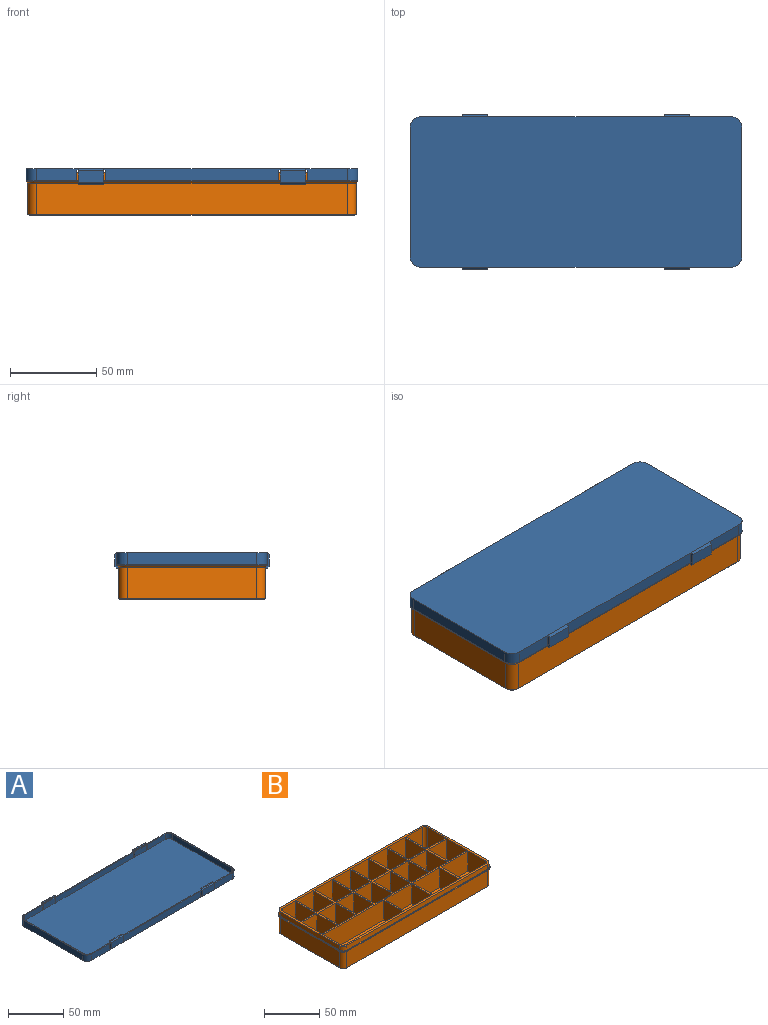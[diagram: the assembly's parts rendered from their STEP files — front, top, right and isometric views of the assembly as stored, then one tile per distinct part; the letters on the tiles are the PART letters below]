
ASSEMBLY  parts=2 mates=1
PART A: 82 faces, bbox 192x89.4x9 mm
  f0: plane 6x1mm, normal (-1,0,0), area 6mm2, adj f14,f18,f39,f43
  f1: plane 6x1mm, normal (1,0,0), area 6mm2, adj f21,f24,f30,f43
  f2: plane 6x1mm, normal (1,0,0), area 6mm2, adj f21,f29,f31,f43
  f3: plane 6x1mm, normal (-1,0,0), area 6mm2, adj f17,f18,f41,f43
  f4: plane 9x2.2mm, normal (-1,0,0), area 16.7mm2, adj f13,f28,f31,f43,f54,f58,f63,f75
  f5: plane 9x2.2mm, normal (1,0,0), area 16.7mm2, adj f13,f16,f28,f43,f54,f58,f63,f75
  f6: plane 9x2.2mm, normal (-1,0,0), area 16.7mm2, adj f12,f16,f26,f43,f55,f59,f62,f72
  f7: plane 6x1mm, normal (-1,0,0), area 6mm2, adj f16,f19,f27,f43
  f8: plane 6x1mm, normal (1,0,0), area 6mm2, adj f16,f19,f27,f43
  f9: plane 9x2.2mm, normal (1,0,0), area 16.7mm2, adj f12,f17,f26,f43,f55,f59,f62,f72
  f10: plane 15x0.6mm, normal (0,1,0), area 9mm2, adj f49,f52,f56,f68
  f11: plane 15x0.6mm, normal (0,1,0), area 9mm2, adj f48,f50,f57,f69
  f12: plane 15x0.6mm, normal (0,-1,0), area 9mm2, adj f6,f9,f55,f73
  f13: plane 15x0.6mm, normal (0,-1,0), area 9mm2, adj f4,f5,f54,f76
  f14: plane 24x7mm, normal (0,-1,0), area 162mm2, adj f0,f18,f34,f35,f43,f48
  f15: plane 102x7mm, normal (0,-1,0), area 702mm2, adj f20,f34,f43,f50,f51,f52,f53
  f16: plane 102x7mm, normal (0,1,0), area 702mm2, adj f5,f6,f7,f8,f19,f34,f43
  f17: plane 24x7mm, normal (0,1,0), area 162mm2, adj f3,f9,f18,f34,f36,f43
  f18: plane 87x29mm, normal (0,0,1), area 138.3mm2, adj f0,f3,f14,f17,f32,f35,f36,f39
  f19: plane 100x1mm, normal (0,0,1), area 100mm2, adj f7,f8,f16,f27
  f20: plane 100x1mm, normal (0,0,1), area 100mm2, adj f15,f23,f51,f53
  f21: plane 87x29mm, normal (0,0,1), area 138.3mm2, adj f1,f2,f24,f29,f30,f31,f33,f37
  f22: plane 15x6mm, normal (0,1,0), area 90mm2, adj f43,f49,f52,f66
  f23: plane 100x6mm, normal (0,1,0), area 600mm2, adj f20,f43,f51,f53
  f24: plane 23x6mm, normal (0,1,0), area 138mm2, adj f1,f21,f43,f47
  f25: plane 15x6mm, normal (0,1,0), area 90mm2, adj f43,f48,f50,f71
  f26: plane 15x6mm, normal (0,-1,0), area 90mm2, adj f6,f9,f43,f74
  f27: plane 100x6mm, normal (0,-1,0), area 600mm2, adj f7,f8,f19,f43
  f28: plane 15x6mm, normal (0,-1,0), area 90mm2, adj f4,f5,f43,f75
  f29: plane 23x6mm, normal (0,-1,0), area 138mm2, adj f2,f21,f43,f46
  f30: plane 24x7mm, normal (0,-1,0), area 162mm2, adj f1,f21,f34,f38,f43,f49
  f31: plane 24x7mm, normal (0,1,0), area 162mm2, adj f2,f4,f21,f34,f37,f43
  f32: plane 75x7mm, normal (1,0,0), area 525mm2, adj f18,f34,f35,f36
  f33: plane 75x7mm, normal (-1,0,0), area 525mm2, adj f21,f34,f37,f38
  f34: plane 192x87mm, normal (0,0,-1), area 16673.1mm2, adj f14,f15,f16,f17,f30,f31,f32,f33
  f35: cylinder r=6mm len=7mm, axis (0,0,1), area 66mm2, adj f14,f18,f32,f34
  f36: cylinder r=6mm len=7mm, axis (0,0,-1), area 66mm2, adj f17,f18,f32,f34
  f37: cylinder r=6mm len=7mm, axis (0,0,1), area 66mm2, adj f21,f31,f33,f34
  f38: cylinder r=6mm len=7mm, axis (0,0,-1), area 66mm2, adj f21,f30,f33,f34
  f39: plane 23x6mm, normal (0,1,0), area 138mm2, adj f0,f18,f43,f44
  f40: plane 75x6mm, normal (-1,0,0), area 450mm2, adj f18,f43,f44,f45
  f41: plane 23x6mm, normal (0,-1,0), area 138mm2, adj f3,f18,f43,f45
  f42: plane 75x6mm, normal (1,0,0), area 450mm2, adj f21,f43,f46,f47
  f43: plane 190x87mm, normal (0,0,1), area 16136.5mm2, adj f0,f1,f2,f3,f4,f5,f6,f7
  f44: cylinder r=5mm len=6mm, axis (0,0,1), area 47.1mm2, adj f18,f39,f40,f43
  f45: cylinder r=5mm len=6mm, axis (0,0,-1), area 47.1mm2, adj f18,f40,f41,f43
  f46: cylinder r=5mm len=6mm, axis (0,0,1), area 47.1mm2, adj f21,f29,f42,f43
  f47: cylinder r=5mm len=6mm, axis (0,0,-1), area 47.1mm2, adj f21,f24,f42,f43
  f48: plane 9x2.2mm, normal (1,0,0), area 16.7mm2, adj f11,f14,f25,f43,f57,f61,f64,f69
  f49: plane 9x2.2mm, normal (-1,0,0), area 16.7mm2, adj f10,f22,f30,f43,f56,f60,f65,f66
  f50: plane 9x2.2mm, normal (-1,0,0), area 16.7mm2, adj f11,f15,f25,f43,f57,f61,f64,f69
  f51: plane 6x1mm, normal (1,0,0), area 6mm2, adj f15,f20,f23,f43
  f52: plane 9x2.2mm, normal (1,0,0), area 16.7mm2, adj f10,f15,f22,f43,f56,f60,f65,f66
  f53: plane 6x1mm, normal (-1,0,0), area 6mm2, adj f15,f20,f23,f43
  f54: plane 15x1.2mm, normal (0,0,1), area 18mm2, adj f4,f5,f13,f78
  f55: plane 15x1.2mm, normal (0,0,1), area 18mm2, adj f6,f9,f12,f79
  f56: plane 15x1.2mm, normal (0,0,1), area 18mm2, adj f10,f49,f52,f80
  f57: plane 15x1.2mm, normal (0,0,1), area 18mm2, adj f11,f48,f50,f81
  f58: plane 15x6.8mm, normal (0,1,0), area 102mm2, adj f4,f5,f63,f78
  f59: plane 15x6.8mm, normal (0,1,0), area 102mm2, adj f6,f9,f62,f79
  f60: plane 15x6.8mm, normal (0,-1,0), area 102mm2, adj f49,f52,f65,f80
  f61: plane 15x6.8mm, normal (0,-1,0), area 102mm2, adj f48,f50,f64,f81
  f62: plane 15x1.2mm, normal (0,0.71,-0.71), area 25.5mm2, adj f6,f9,f34,f59
  f63: plane 15x1.2mm, normal (0,0.71,-0.71), area 25.5mm2, adj f4,f5,f34,f58
  f64: plane 15x1.2mm, normal (0,-0.71,-0.71), area 25.5mm2, adj f34,f48,f50,f61
  f65: plane 15x1.2mm, normal (0,-0.71,-0.71), area 25.5mm2, adj f34,f49,f52,f60
  f66: plane 15x1mm, normal (0,0,1), area 15mm2, adj f22,f49,f52,f67
  f67: plane 15x0.4mm, normal (0,1,0), area 6mm2, adj f49,f52,f66,f68
  f68: plane 15x1mm, normal (0,0.71,-0.71), area 21.2mm2, adj f10,f49,f52,f67
  f69: plane 15x1mm, normal (0,0.71,-0.71), area 21.2mm2, adj f11,f48,f50,f70
  f70: plane 15x0.4mm, normal (0,1,0), area 6mm2, adj f48,f50,f69,f71
  f71: plane 15x1mm, normal (0,0,1), area 15mm2, adj f25,f48,f50,f70
  f72: plane 15x0.4mm, normal (0,-1,0), area 6mm2, adj f6,f9,f73,f74
  f73: plane 15x1mm, normal (0,-0.71,-0.71), area 21.2mm2, adj f6,f9,f12,f72
  f74: plane 15x1mm, normal (0,0,1), area 15mm2, adj f6,f9,f26,f72
  f75: plane 15x1mm, normal (0,0,1), area 15mm2, adj f4,f5,f28,f77
  f76: plane 15x1mm, normal (0,-0.71,-0.71), area 21.2mm2, adj f4,f5,f13,f77
  f77: plane 15x0.4mm, normal (0,-1,0), area 6mm2, adj f4,f5,f75,f76
  f78: plane 15x1mm, normal (0,0.71,0.71), area 21.2mm2, adj f4,f5,f54,f58
  f79: plane 15x1mm, normal (0,0.71,0.71), area 21.2mm2, adj f6,f9,f55,f59
  f80: plane 15x1mm, normal (0,-0.71,0.71), area 21.2mm2, adj f49,f52,f56,f60
  f81: plane 15x1mm, normal (0,-0.71,0.71), area 21.2mm2, adj f48,f50,f57,f61
PART B: 134 faces, bbox 192x87x25 mm
  f0: plane 34.45x25.93mm, normal (0,0,1), area 891.5mm2, adj f2,f44,f57,f65,f99
  f1: plane 34.45x22.2mm, normal (0,-1,0), area 764.8mm2, adj f3,f61,f97,f98
  f2: plane 180x23mm, normal (0,1,0), area 4033.4mm2, adj f0,f3,f5,f47,f56,f57,f60,f61
  f3: plane 34.45x25.93mm, normal (0,0,1), area 893.4mm2, adj f1,f2,f97,f98
  f4: plane 34.45x22.2mm, normal (0,-1,0), area 764.8mm2, adj f5,f61,f95,f96
  f5: plane 34.45x25.93mm, normal (0,0,1), area 893.4mm2, adj f2,f4,f95,f96
  f6: plane 77.85x22.2mm, normal (0,-1,0), area 1728.3mm2, adj f45,f56,f61,f94
  f7: plane 25.93x23.5mm, normal (0,0,1), area 609.4mm2, adj f44,f63,f64,f90
  f8: plane 25.93x23.5mm, normal (0,0,1), area 607.5mm2, adj f10,f44,f58,f62,f92
  f9: plane 22.2x21.9mm, normal (0,1,0), area 486.2mm2, adj f13,f61,f86,f91
  f10: plane 180x23mm, normal (0,-1,0), area 3891.4mm2, adj f8,f14,f19,f24,f29,f34,f39,f46
  f11: plane 22.2x21.9mm, normal (0,1,0), area 486.2mm2, adj f14,f61,f88,f93
  f12: plane 22.2x21.9mm, normal (0,-1,0), area 486.2mm2, adj f13,f61,f86,f91
  f13: plane 25.93x21.9mm, normal (0,0,1), area 567.9mm2, adj f9,f12,f86,f91
  f14: plane 25.93x21.9mm, normal (0,0,1), area 567.9mm2, adj f10,f11,f88,f93
  f15: plane 22.2x21.9mm, normal (0,1,0), area 486.2mm2, adj f18,f61,f82,f87
  f16: plane 22.2x21.9mm, normal (0,1,0), area 486.2mm2, adj f19,f61,f84,f89
  f17: plane 22.2x21.9mm, normal (0,-1,0), area 486.2mm2, adj f18,f61,f82,f87
  f18: plane 25.93x21.9mm, normal (0,0,1), area 567.9mm2, adj f15,f17,f82,f87
  f19: plane 25.93x21.9mm, normal (0,0,1), area 567.9mm2, adj f10,f16,f84,f89
  f20: plane 22.2x21.9mm, normal (0,1,0), area 486.2mm2, adj f23,f61,f78,f83
  f21: plane 22.2x21.9mm, normal (0,1,0), area 486.2mm2, adj f24,f61,f80,f85
  f22: plane 22.2x21.9mm, normal (0,-1,0), area 486.2mm2, adj f23,f61,f78,f83
  f23: plane 25.93x21.9mm, normal (0,0,1), area 567.9mm2, adj f20,f22,f78,f83
  f24: plane 25.93x21.9mm, normal (0,0,1), area 567.9mm2, adj f10,f21,f80,f85
  f25: plane 22.2x21.9mm, normal (0,1,0), area 486.2mm2, adj f28,f61,f74,f79
  f26: plane 22.2x21.9mm, normal (0,1,0), area 486.2mm2, adj f29,f61,f76,f81
  f27: plane 22.2x21.9mm, normal (0,-1,0), area 486.2mm2, adj f28,f61,f74,f79
  f28: plane 25.93x21.9mm, normal (0,0,1), area 567.9mm2, adj f25,f27,f74,f79
  f29: plane 25.93x21.9mm, normal (0,0,1), area 567.9mm2, adj f10,f26,f76,f81
  f30: plane 22.2x21.9mm, normal (0,1,0), area 486.2mm2, adj f33,f61,f70,f75
  f31: plane 22.2x21.9mm, normal (0,1,0), area 486.2mm2, adj f34,f61,f72,f77
  f32: plane 22.2x21.9mm, normal (0,-1,0), area 486.2mm2, adj f33,f61,f70,f75
  f33: plane 25.93x21.9mm, normal (0,0,1), area 567.9mm2, adj f30,f32,f70,f75
  f34: plane 25.93x21.9mm, normal (0,0,1), area 567.9mm2, adj f10,f31,f72,f77
  f35: plane 22.2x21.9mm, normal (0,1,0), area 486.2mm2, adj f38,f61,f66,f71
  f36: plane 22.2x21.9mm, normal (0,1,0), area 486.2mm2, adj f39,f61,f69,f73
  f37: plane 22.2x21.9mm, normal (0,-1,0), area 486.2mm2, adj f38,f61,f66,f71
  f38: plane 25.93x21.9mm, normal (0,0,1), area 567.9mm2, adj f35,f37,f66,f71
  f39: plane 25.93x21.9mm, normal (0,0,1), area 567.9mm2, adj f10,f36,f69,f73
  f40: plane 22.2x19.9mm, normal (0,1,0), area 441.8mm2, adj f43,f45,f61,f67
  f41: plane 22.2x19.9mm, normal (0,1,0), area 441.8mm2, adj f45,f46,f61,f68
  f42: plane 22.2x19.9mm, normal (0,-1,0), area 441.8mm2, adj f43,f45,f61,f67
  f43: plane 25.93x19.9mm, normal (0,0,1), area 516.1mm2, adj f40,f42,f45,f67
  f44: plane 75x23mm, normal (-1,0,0), area 1654mm2, adj f0,f7,f8,f47,f57,f58,f61,f62
  f45: plane 75x23mm, normal (1,0,0), area 1654mm2, adj f6,f40,f41,f42,f43,f46,f47,f56
  f46: plane 25.93x19.9mm, normal (0,0,1), area 514.1mm2, adj f10,f41,f45,f59,f68
  f47: plane 190x85mm, normal (0,0,1), area 1070.3mm2, adj f2,f10,f44,f45,f48,f49,f50,f51
  f48: plane 180x5mm, normal (0,-1,0), area 900mm2, adj f47,f52,f55,f114
  f49: plane 75x5mm, normal (1,0,0), area 375mm2, adj f47,f52,f53,f114
  f50: plane 180x5mm, normal (0,1,0), area 900mm2, adj f47,f53,f54,f114
  f51: plane 75x5mm, normal (-1,0,0), area 375mm2, adj f47,f54,f55,f114
  f52: cylinder r=5mm len=5mm, axis (0,0,1), area 39.3mm2, adj f47,f48,f49,f114
  f53: cylinder r=5mm len=5mm, axis (0,0,-1), area 39.3mm2, adj f47,f49,f50,f114
  f54: cylinder r=5mm len=5mm, axis (0,0,1), area 39.3mm2, adj f47,f50,f51,f114
  f55: cylinder r=5mm len=5mm, axis (0,0,-1), area 39.3mm2, adj f47,f48,f51,f114
  f56: plane 77.85x25.93mm, normal (0,0,1), area 2017mm2, adj f2,f6,f45,f60,f94
  f57: cylinder r=3mm len=23mm, axis (0,0,1), area 108.4mm2, adj f0,f2,f44,f47
  f58: cylinder r=3mm len=23mm, axis (0,0,-1), area 108.4mm2, adj f8,f10,f44,f47
  f59: cylinder r=3mm len=23mm, axis (0,0,1), area 108.4mm2, adj f10,f45,f46,f47
  f60: cylinder r=3mm len=23mm, axis (0,0,-1), area 108.4mm2, adj f2,f45,f47,f56
  f61: plane 186x81mm, normal (0,0,1), area 1300.6mm2, adj f1,f2,f4,f6,f9,f10,f11,f12
  f62: plane 23.5x22.2mm, normal (0,1,0), area 521.7mm2, adj f8,f44,f61,f92
  f63: plane 23.5x22.2mm, normal (0,-1,0), area 521.7mm2, adj f7,f44,f61,f90
  f64: plane 23.5x22.2mm, normal (0,1,0), area 521.7mm2, adj f7,f44,f61,f90
  f65: plane 34.45x22.2mm, normal (0,-1,0), area 764.8mm2, adj f0,f44,f61,f99
  f66: plane 25.93x22.2mm, normal (1,0,0), area 575.7mm2, adj f35,f37,f38,f61
  f67: plane 25.93x22.2mm, normal (-1,0,0), area 575.7mm2, adj f40,f42,f43,f61
  f68: plane 25.93x22.2mm, normal (-1,0,0), area 575.7mm2, adj f10,f41,f46,f61
  f69: plane 25.93x22.2mm, normal (1,0,0), area 575.7mm2, adj f10,f36,f39,f61
  f70: plane 25.93x22.2mm, normal (1,0,0), area 575.7mm2, adj f30,f32,f33,f61
  f71: plane 25.93x22.2mm, normal (-1,0,0), area 575.7mm2, adj f35,f37,f38,f61
  f72: plane 25.93x22.2mm, normal (1,0,0), area 575.7mm2, adj f10,f31,f34,f61
  f73: plane 25.93x22.2mm, normal (-1,0,0), area 575.7mm2, adj f10,f36,f39,f61
  f74: plane 25.93x22.2mm, normal (1,0,0), area 575.7mm2, adj f25,f27,f28,f61
  f75: plane 25.93x22.2mm, normal (-1,0,0), area 575.7mm2, adj f30,f32,f33,f61
  f76: plane 25.93x22.2mm, normal (1,0,0), area 575.7mm2, adj f10,f26,f29,f61
  f77: plane 25.93x22.2mm, normal (-1,0,0), area 575.7mm2, adj f10,f31,f34,f61
  f78: plane 25.93x22.2mm, normal (1,0,0), area 575.7mm2, adj f20,f22,f23,f61
  f79: plane 25.93x22.2mm, normal (-1,0,0), area 575.7mm2, adj f25,f27,f28,f61
  f80: plane 25.93x22.2mm, normal (1,0,0), area 575.7mm2, adj f10,f21,f24,f61
  f81: plane 25.93x22.2mm, normal (-1,0,0), area 575.7mm2, adj f10,f26,f29,f61
  f82: plane 25.93x22.2mm, normal (1,0,0), area 575.7mm2, adj f15,f17,f18,f61
  f83: plane 25.93x22.2mm, normal (-1,0,0), area 575.7mm2, adj f20,f22,f23,f61
  f84: plane 25.93x22.2mm, normal (1,0,0), area 575.7mm2, adj f10,f16,f19,f61
  f85: plane 25.93x22.2mm, normal (-1,0,0), area 575.7mm2, adj f10,f21,f24,f61
  f86: plane 25.93x22.2mm, normal (1,0,0), area 575.7mm2, adj f9,f12,f13,f61
  f87: plane 25.93x22.2mm, normal (-1,0,0), area 575.7mm2, adj f15,f17,f18,f61
  f88: plane 25.93x22.2mm, normal (1,0,0), area 575.7mm2, adj f10,f11,f14,f61
  f89: plane 25.93x22.2mm, normal (-1,0,0), area 575.7mm2, adj f10,f16,f19,f61
  f90: plane 25.93x22.2mm, normal (1,0,0), area 575.7mm2, adj f7,f61,f63,f64
  f91: plane 25.93x22.2mm, normal (-1,0,0), area 575.7mm2, adj f9,f12,f13,f61
  f92: plane 25.93x22.2mm, normal (1,0,0), area 575.7mm2, adj f8,f10,f61,f62
  f93: plane 25.93x22.2mm, normal (-1,0,0), area 575.7mm2, adj f10,f11,f14,f61
  f94: plane 25.93x22.2mm, normal (-1,0,0), area 575.7mm2, adj f2,f6,f56,f61
  f95: plane 25.93x22.2mm, normal (1,0,0), area 575.7mm2, adj f2,f4,f5,f61
  f96: plane 25.93x22.2mm, normal (-1,0,0), area 575.7mm2, adj f2,f4,f5,f61
  f97: plane 25.93x22.2mm, normal (1,0,0), area 575.7mm2, adj f1,f2,f3,f61
  f98: plane 25.93x22.2mm, normal (-1,0,0), area 575.7mm2, adj f1,f2,f3,f61
  f99: plane 25.93x22.2mm, normal (1,0,0), area 575.7mm2, adj f0,f2,f61,f65
  f100: cylinder r=6mm len=6mm, axis (0,0,-1), area 3.8mm2, adj f101,f102,f114,f115
  f101: cone r=5mm half-angle=45deg, axis (0,0,1), area 12.2mm2, adj f100,f103,f116,f128
  f102: plane 75x0.4mm, normal (-1,0,0), area 30mm2, adj f100,f103,f104,f114
  f103: plane 75x1mm, normal (-0.71,0,-0.71), area 106.1mm2, adj f101,f102,f105,f130
  f104: cylinder r=6mm len=6mm, axis (0,0,-1), area 3.8mm2, adj f102,f105,f106,f114
  f105: cone r=5mm half-angle=45deg, axis (0,0,1), area 12.2mm2, adj f103,f104,f107,f129
  f106: plane 180x0.4mm, normal (0,-1,0), area 72mm2, adj f104,f107,f108,f114
  f107: plane 180x1mm, normal (0,-0.71,-0.71), area 254.6mm2, adj f105,f106,f109,f133
  f108: cylinder r=6mm len=6mm, axis (0,0,-1), area 3.8mm2, adj f106,f109,f110,f114
  f109: cone r=5mm half-angle=45deg, axis (0,0,1), area 12.2mm2, adj f107,f108,f111,f126
  f110: plane 75x0.4mm, normal (1,0,0), area 30mm2, adj f108,f111,f112,f114
  f111: plane 75x1mm, normal (0.71,0,-0.71), area 106.1mm2, adj f109,f110,f113,f132
  f112: cylinder r=6mm len=6mm, axis (0,0,-1), area 3.8mm2, adj f110,f113,f114,f115
  f113: cone r=5mm half-angle=45deg, axis (0,0,1), area 12.2mm2, adj f111,f112,f116,f127
  f114: plane 192x87mm, normal (0,0,1), area 544.6mm2, adj f48,f49,f50,f51,f52,f53,f54,f55
  f115: plane 180x0.4mm, normal (0,1,0), area 72mm2, adj f100,f112,f114,f116
  f116: plane 180x1mm, normal (0,0.71,-0.71), area 254.6mm2, adj f101,f113,f115,f131
  f117: plane 188.8x83.8mm, normal (0,0,-1), area 15804.8mm2, adj f118,f119,f120,f121,f122,f123,f124,f125
  f118: plane 180x0.6mm, normal (0,-0.71,-0.71), area 152.7mm2, adj f117,f122,f125,f133
  f119: plane 75x0.6mm, normal (0.71,0,-0.71), area 63.6mm2, adj f117,f122,f123,f132
  f120: plane 180x0.6mm, normal (0,0.71,-0.71), area 152.7mm2, adj f117,f123,f124,f131
  f121: plane 75x0.6mm, normal (-0.71,0,-0.71), area 63.6mm2, adj f117,f124,f125,f130
  f122: cone r=4.4mm half-angle=45deg, axis (0,0,1), area 6.3mm2, adj f117,f118,f119,f126
  f123: cone r=4.4mm half-angle=45deg, axis (0,0,1), area 6.3mm2, adj f117,f119,f120,f127
  f124: cone r=4.4mm half-angle=45deg, axis (0,0,1), area 6.3mm2, adj f117,f120,f121,f128
  f125: cone r=4.4mm half-angle=45deg, axis (0,0,1), area 6.3mm2, adj f117,f118,f121,f129
  f126: cylinder r=5mm len=18mm, axis (0,0,1), area 141.4mm2, adj f109,f122,f132,f133
  f127: cylinder r=5mm len=18mm, axis (0,0,-1), area 141.4mm2, adj f113,f123,f131,f132
  f128: cylinder r=5mm len=18mm, axis (0,0,1), area 141.4mm2, adj f101,f124,f130,f131
  f129: cylinder r=5mm len=18mm, axis (0,0,-1), area 141.4mm2, adj f105,f125,f130,f133
  f130: plane 75x18mm, normal (-1,0,0), area 1350mm2, adj f103,f121,f128,f129
  f131: plane 180x18mm, normal (0,1,0), area 3240mm2, adj f116,f120,f127,f128
  f132: plane 75x18mm, normal (1,0,0), area 1350mm2, adj f111,f119,f126,f127
  f133: plane 180x18mm, normal (0,-1,0), area 3240mm2, adj f107,f118,f126,f129
PLACE A rot(axis=(0,1,0),180deg) t=(0,0,27)mm
PLACE B at identity
MATE fastened B.f52 <-> A.f38  axis (0,0,1) through (90,-37.5,20)mm
